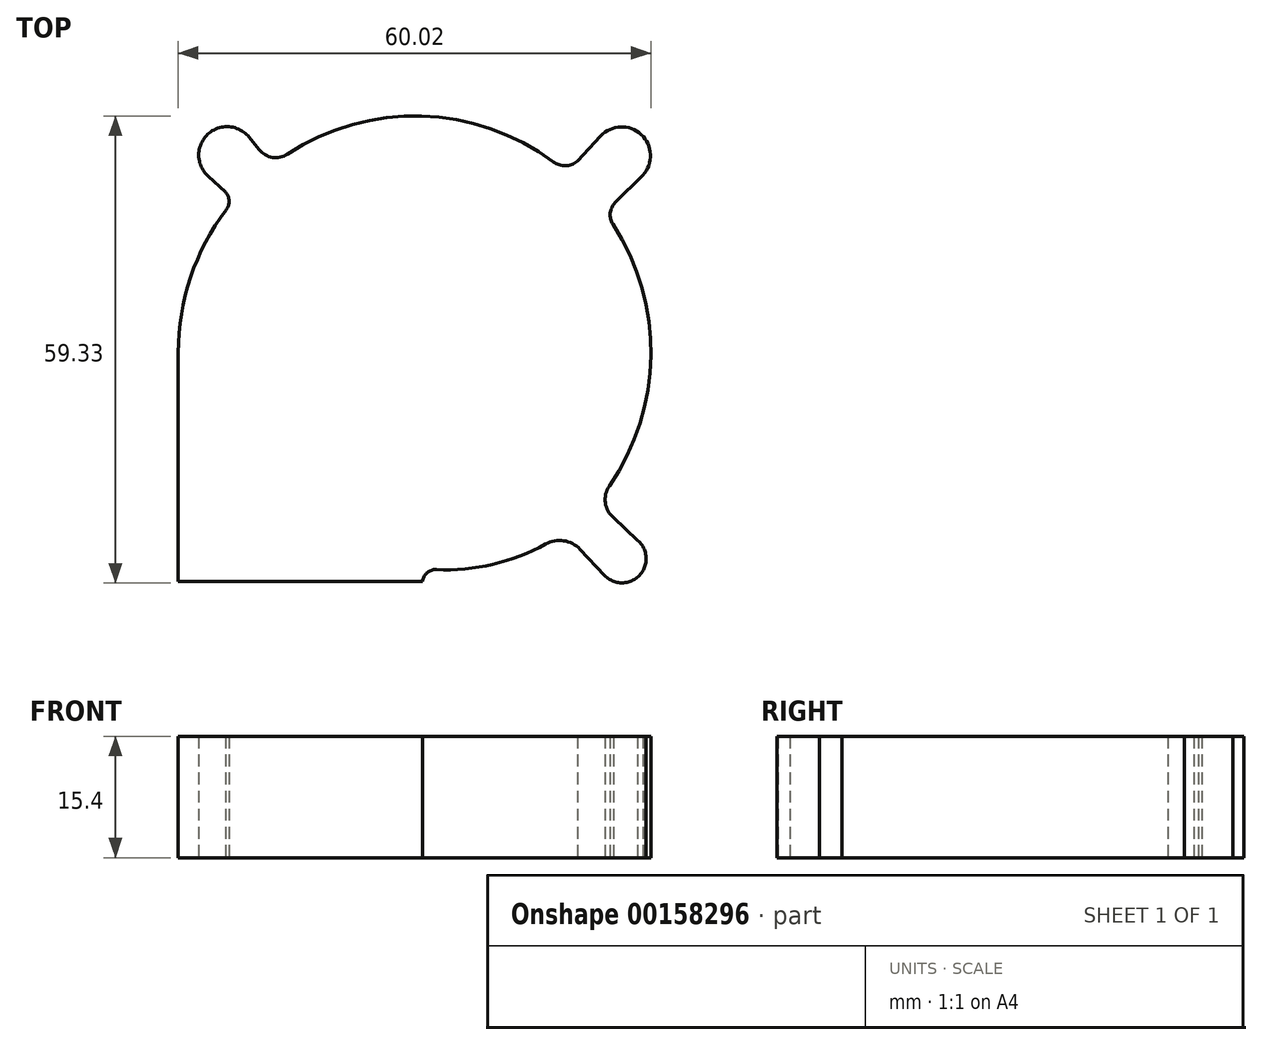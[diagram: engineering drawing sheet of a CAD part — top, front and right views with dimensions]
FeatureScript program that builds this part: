
annotation { "Feature Type Name" : "Feature", "Feature Type Description" : "" }
export const myFeature = defineFeature(function(context is Context, id is Id, definition is map)
    precondition{}
    {
        {
            var Q0;
            Q0=qCreatedBy(makeId("Top.planeOp"),FACE);
            var sketch = newSketch(context, id + "F0", { "sketchPlane" : qUnion([Q0])});
            skLineSegment(sketch, "E0", {"start": v(-17.9, -44.83) * mm, "end": v(-17.9, -15.73) * mm});
            skArc(sketch, "E1", {"start": v(-17.9, -15.73) * mm, "mid": v(23.68, 11.95) * mm, "end": v(33.17, -37.09) * mm});
            skLineSegment(sketch, "E2", {"start": v(13.1, -44.83) * mm, "end": v(-17.9, -44.83) * mm});
            skFitSpline(sketch, "E3", {"points": [v(14.87, -43.27) * mm, v(33.17, -37.09) * mm], "startDerivative": vector(18.86, -1.59) * mm, "endDerivative": vector(11.1, 10.22) * mm});
            skFitSpline(sketch, "E4", {"points": [v(13.1, -44.83) * mm, v(14.87, -43.27) * mm], "startDerivative": vector(0.09, 3.1) * mm, "endDerivative": vector(4.63, -0.46) * mm});
            skCircle(sketch, "E5", {"center": v(38.3, -41.8) * mm, "radius": 2.25 * mm});
            skCircle(sketch, "E6", {"center": v(-11.7, 9.27) * mm, "radius": 2.8 * mm});
            skCircle(sketch, "E7.0.1.0", {"center": v(38.3, 9.26) * mm, "radius": 2.8 * mm});
            skSolve(sketch);
        }
        {
            var Q0;
            Q0=makeQuery(id+"F0.imprint","IMPRINT",FACE,{"disambiguationData":[TD([[makeQuery(id+"F0.imprint","IMPRINT",EDGE,{"derivedFrom":sQuery(id+"F0.wireOp",EDGE,"E0")}),-1.0]])]});
            var sketch = newSketch(context, id + "F1", { "sketchPlane" : qUnion([Q0])});
            skLineSegment(sketch, "E8", {"start": v(-17.9, -44.8) * mm, "end": v(-17.9, -15.7) * mm});
            skLineSegment(sketch, "E9", {"start": v(-17.9, -44.8) * mm, "end": v(13.12, -44.8) * mm});
            skArc(sketch, "E10", {"start": v(-17.9, -15.7) * mm, "mid": v(-16.34, -6.14) * mm, "end": v(-11.83, 2.42) * mm});
            skArc(sketch, "E11", {"start": v(-11.83, 2.42) * mm, "mid": v(-11.47, 3.57) * mm, "end": v(-11.91, 4.7) * mm});
            skLineSegment(sketch, "E12", {"start": v(-11.91, 4.7) * mm, "end": v(-14.14, 6.73) * mm});
            skArc(sketch, "E13", {"start": v(-14.14, 6.73) * mm, "mid": v(-14.17, 12.02) * mm, "end": v(-8.9, 11.64) * mm});
            skLineSegment(sketch, "E14", {"start": v(-8.9, 11.64) * mm, "end": v(-7.65, 10.07) * mm});
            skArc(sketch, "E15", {"start": v(-7.65, 10.07) * mm, "mid": v(-5.95, 9.09) * mm, "end": v(-4.04, 9.5) * mm});
            skArc(sketch, "E16", {"start": v(-4.04, 9.5) * mm, "mid": v(13, 14.35) * mm, "end": v(29.73, 8.52) * mm});
            skArc(sketch, "E17", {"start": v(29.73, 8.52) * mm, "mid": v(31.28, 8.03) * mm, "end": v(32.8, 8.59) * mm});
            skLineSegment(sketch, "E18", {"start": v(32.8, 8.59) * mm, "end": v(35.74, 11.78) * mm});
            skArc(sketch, "E19", {"start": v(35.74, 11.78) * mm, "mid": v(40.9, 11.99) * mm, "end": v(41.1, 6.83) * mm});
            skLineSegment(sketch, "E20", {"start": v(41.1, 6.83) * mm, "end": v(37.59, 3.32) * mm});
            skArc(sketch, "E21", {"start": v(37.59, 3.32) * mm, "mid": v(36.96, 2) * mm, "end": v(37.3, 0.6) * mm});
            skLineSegment(sketch, "E22", {"start": v(40.43, -39.56) * mm, "end": v(37.4, -36.69) * mm});
            skLineSegment(sketch, "E23", {"start": v(36.22, -44) * mm, "end": v(33.13, -40.7) * mm});
            skArc(sketch, "E24", {"start": v(36.22, -44) * mm, "mid": v(40.68, -44.01) * mm, "end": v(40.43, -39.56) * mm});
            skArc(sketch, "E25", {"start": v(37.3, 0.6) * mm, "mid": v(42.12, -16.1) * mm, "end": v(36.84, -32.67) * mm});
            skArc(sketch, "E26", {"start": v(36.84, -32.67) * mm, "mid": v(36.34, -34.8) * mm, "end": v(37.4, -36.69) * mm});
            skArc(sketch, "E27", {"start": v(33.13, -40.7) * mm, "mid": v(31.06, -39.62) * mm, "end": v(28.76, -40.03) * mm});
            skArc(sketch, "E28", {"start": v(28.76, -40.03) * mm, "mid": v(22.04, -42.61) * mm, "end": v(14.88, -43.27) * mm});
            skArc(sketch, "E29", {"start": v(14.88, -43.27) * mm, "mid": v(13.7, -43.68) * mm, "end": v(13.12, -44.8) * mm});
            skSolve(sketch);
        }
        {
            var Q0;
            Q0 = qSketchRegion(id + "F1", true);
            extrude(context, id + "F2", {"entities" : qUnion([Q0]), "depth" : 15.4 * mm});
        }
    });
